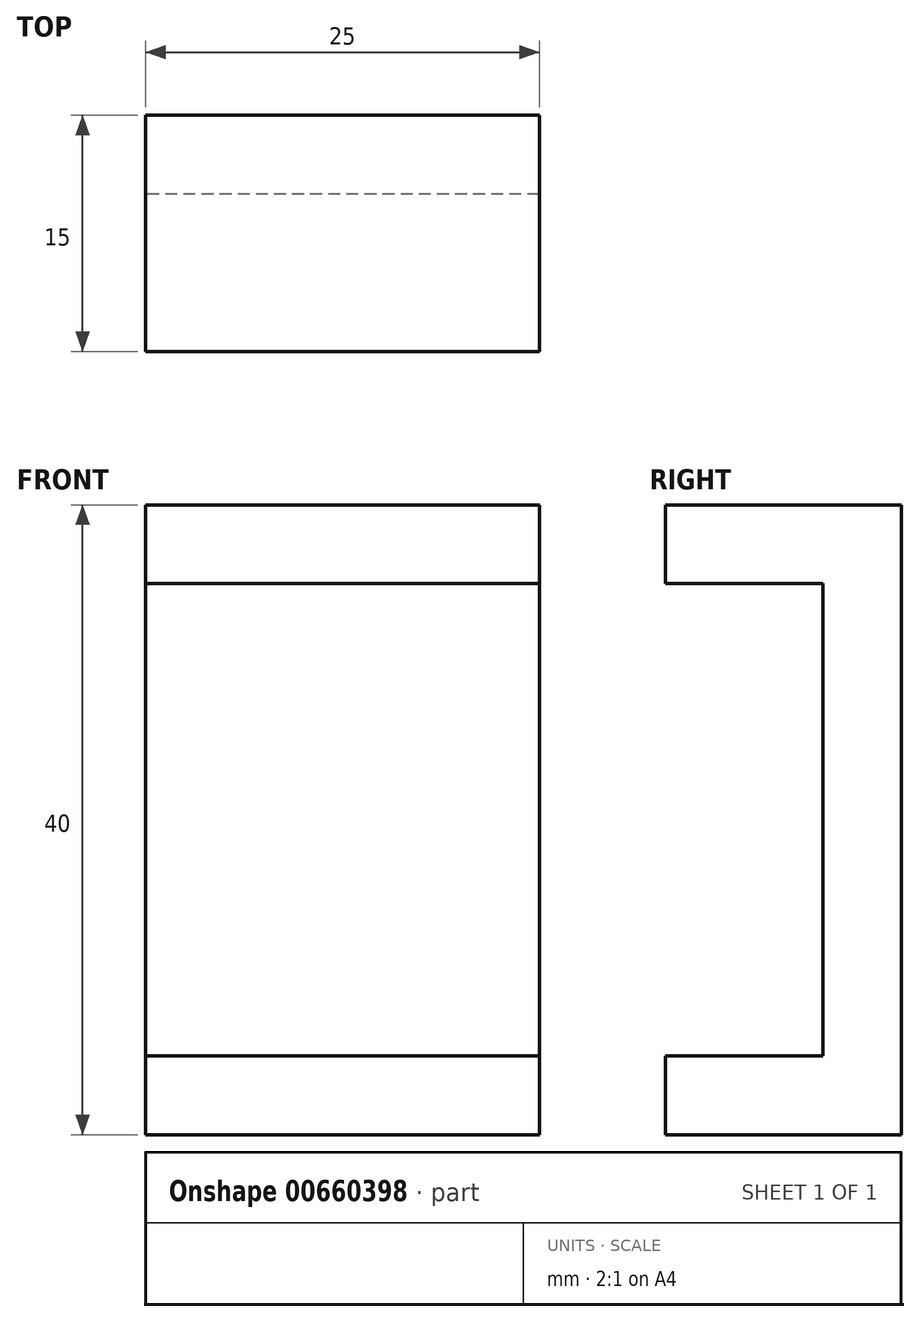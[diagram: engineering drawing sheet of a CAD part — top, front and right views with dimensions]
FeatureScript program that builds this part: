
annotation { "Feature Type Name" : "Feature", "Feature Type Description" : "" }
export const myFeature = defineFeature(function(context is Context, id is Id, definition is map)
    precondition{}
    {
        {
            var Q0;
            Q0=qCreatedBy(makeId("Right.planeOp"),FACE);
            var sketch = newSketch(context, id + "F0", { "sketchPlane" : qUnion([Q0])});
            skLineSegment(sketch, "E0.bottom", {"start": v(0, 0) * mm, "end": v(10, 0) * mm});
            skLineSegment(sketch, "E0.top", {"start": v(0, 30) * mm, "end": v(10, 30) * mm});
            skLineSegment(sketch, "E0.right", {"start": v(10, 0) * mm, "end": v(10, 30) * mm});
            skLineSegment(sketch, "E1.0", {"start": v(0, -5) * mm, "end": v(15, -5) * mm});
            skLineSegment(sketch, "E1.1", {"start": v(15, -5) * mm, "end": v(15, 35) * mm});
            skLineSegment(sketch, "E1.2", {"start": v(0, 35) * mm, "end": v(15, 35) * mm});
            skLineSegment(sketch, "E2", {"start": v(0, 35) * mm, "end": v(0, 30) * mm});
            skLineSegment(sketch, "E3", {"start": v(0, 0) * mm, "end": v(0, -5) * mm});
            skSolve(sketch);
        }
        {
            var Q0;
            Q0=makeQuery(id+"F0.imprint","IMPRINT",FACE,{"disambiguationData":[TD([[makeQuery(id+"F0.imprint","IMPRINT",EDGE,{"derivedFrom":sQuery(id+"F0.wireOp",EDGE,"E0.bottom")}),-1.0]])]});
            extrude(context, id + "F1", {"entities" : qUnion([Q0]), "depth" : 25 * mm, "offsetDistance" : 25 * mm});
        }
    });
